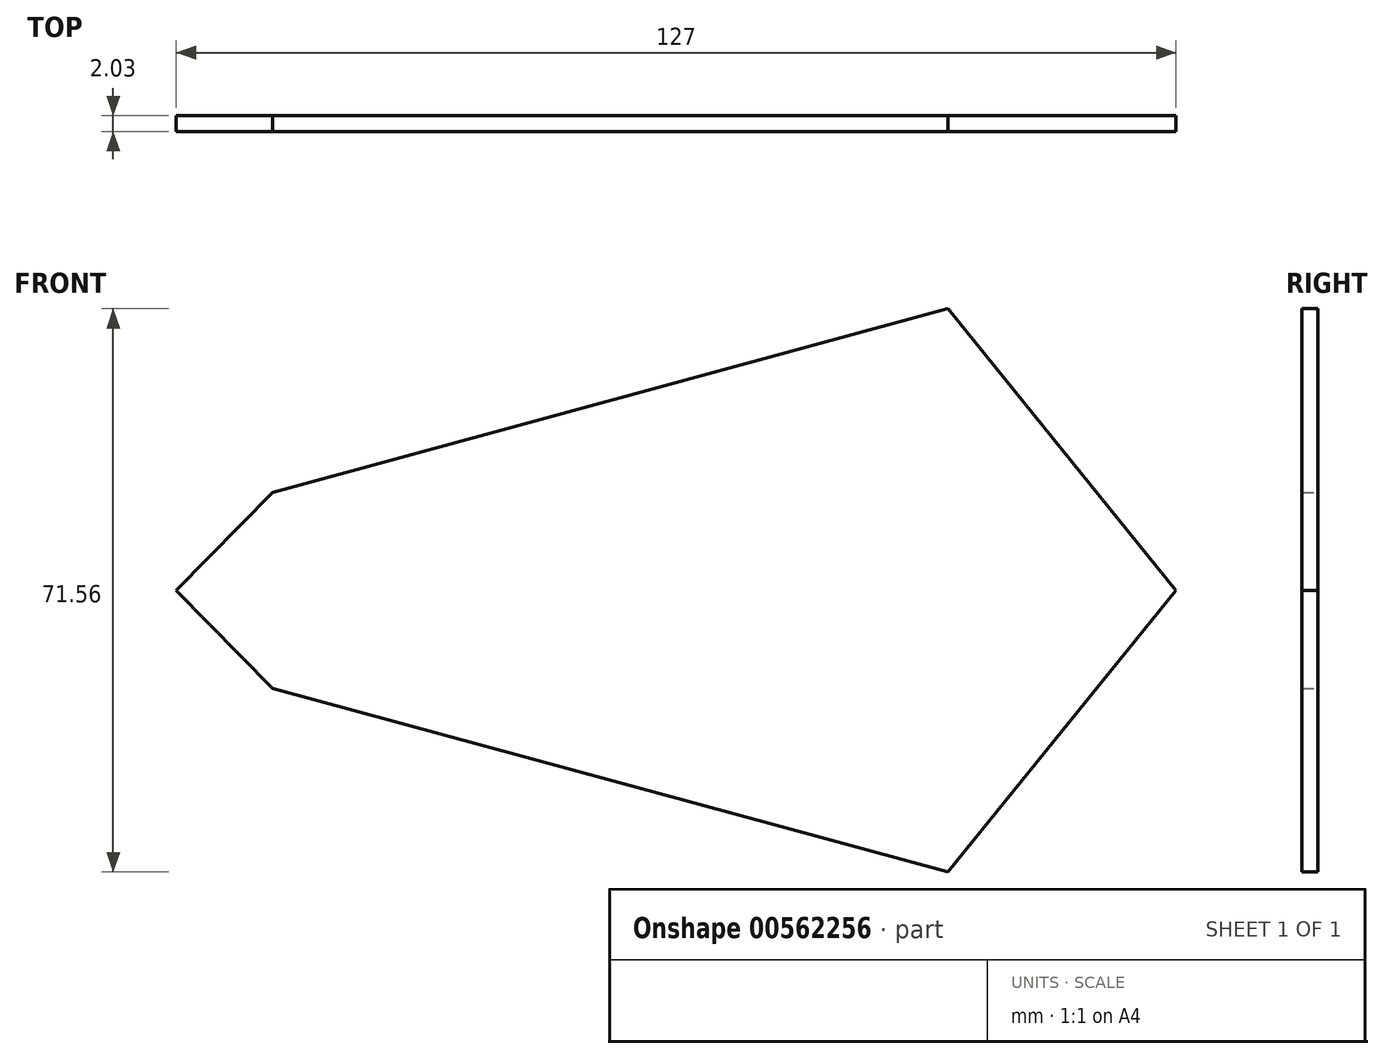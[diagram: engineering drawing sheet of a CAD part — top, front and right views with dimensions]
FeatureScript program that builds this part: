
annotation { "Feature Type Name" : "Feature", "Feature Type Description" : "" }
export const myFeature = defineFeature(function(context is Context, id is Id, definition is map)
    precondition{}
    {
        {
            var Q0;
            Q0=qCreatedBy(makeId("Front.planeOp"),FACE);
            var sketch = newSketch(context, id + "F0", { "sketchPlane" : qUnion([Q0])});
            skLineSegment(sketch, "E0", {"start": v(0, 0) * mm, "end": v(-127, 0) * mm, "construction": true});
            skLineSegment(sketch, "E1", {"start": v(0, 0) * mm, "end": v(-28.97, -35.78) * mm});
            skLineSegment(sketch, "E2", {"start": v(-28.97, -35.78) * mm, "end": v(-114.76, -12.45) * mm});
            skLineSegment(sketch, "E3", {"start": v(-114.76, -12.45) * mm, "end": v(-127, 0) * mm});
            skLineSegment(sketch, "E4.MirrorCS", {"start": v(0, 0) * mm, "end": v(-28.97, 35.78) * mm});
            skLineSegment(sketch, "E5.MirrorCS", {"start": v(-28.97, 35.78) * mm, "end": v(-114.76, 12.45) * mm});
            skLineSegment(sketch, "E6.MirrorCS", {"start": v(-114.76, 12.45) * mm, "end": v(-127, 0) * mm});
            skSolve(sketch);
        }
        {
            var Q0;
            Q0 = qSketchRegion(id + "F0", true);
            extrude(context, id + "F1", {"entities" : qUnion([Q0]), "depth" : 2.03 * mm, "offsetDistance" : 25.4 * mm});
        }
    });
